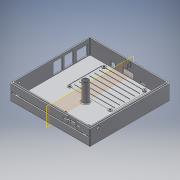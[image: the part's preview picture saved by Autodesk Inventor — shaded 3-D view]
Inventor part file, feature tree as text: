
AUTODESK INVENTOR PART (.ipt)
format: ipt  version: 2018 (Build 220112000, 112)  size: 822,784 bytes
history: native  units: in
note: dims shown in document units (in); Inventor stores cm internally (conversion verified against a paired STEP export)
features: extrude x34, sketch x30, projected_geometry x8, reference x7, fillet x6, plane x6, thread x4, other x3, mirror x1
ambient origin geometry x8: Origin, YZ Plane, XZ Plane, XY Plane, X Axis, Y Axis, Z Axis, Center Point
bodies: Solid1 (feature_tree)
feature tree (99):
  extrude  "Extrusion1"  Depth=4.5in
  extrude  "Extrusion4"  Depth=0.1in
  sketch  "Sketch6"  dims[d12=0.7874in d13=0.0in d17=2.2047in]
  extrude  "Extrusion5"  Depth=2.2047in
  extrude  "Extrusion6"  Depth=0.4035in
  extrude  "Extrusion7"  Depth=0.6299in
  extrude  "Extrusion8"  Depth=0.2589in
  extrude  "Extrusion9"  Depth=0.2589in
  extrude  "Extrusion10"  Depth=0.314in
  extrude  "Extrusion11"  Depth=0.1575in
  extrude  "Extrusion12"  Depth=0.8425in
  thread  "Thread1"  [1 undecoded]
  thread  "Thread2"  [1 undecoded]
  thread  "Thread3"  [1 undecoded]
  thread  "Thread4"  [1 undecoded]
  extrude  "Extrusion13"  Depth=0.689in TaperAngle=0.0deg
  extrude  "Extrusion14"  Depth=0.2953in TaperAngle=0.0deg
  extrude  "Extrusion15"  Depth=0.1378in TaperAngle=0.0deg
  fillet  "Fillet1"  Radius=0.0394in
  extrude  "Extrusion16"  Depth=0.1378in
  extrude  "Extrusion17"  Depth=0.1378in
  fillet  "Fillet3"  Radius=0.1378in
  extrude  "Extrusion18"  Depth=2.2835in
  extrude  "Extrusion19"  Depth=2.2835in
  plane  "Work Plane1"
  extrude  "Extrusion20"  Depth=0.05in
  extrude  "Extrusion21"  Depth=0.05in
  fillet  "Fillet4"  Radius=0.05in
  plane  "Work Plane2"
  extrude  "Extrusion22"  Depth=0.075in TaperAngle=0.0deg
  extrude  "Extrusion23"  Depth=1.0in TaperAngle=0.0deg
  extrude  "Extrusion24"  Depth=1.0in TaperAngle=0.0deg
  extrude  "Extrusion25"  Depth=0.064in
  extrude  "Extrusion26"  Depth=0.05in
  extrude  "Extrusion27"  Depth=0.05in TaperAngle=0.0deg
  extrude  "Extrusion28"  Depth=0.05in TaperAngle=0.0deg
  extrude  "Extrusion29"  Depth=0.05in
  plane  "Work Plane3"
  mirror  "Mirror1"
  sketch  "Sketch27"  dims[d82=0.05in d83=0.0in d84=0.075in]
  plane  "Work Plane4"
  extrude  "Extrusion30"  Depth=0.05in
  extrude  "Extrusion31"  Depth=0.05in TaperAngle=0.0deg
  extrude  "Extrusion32"  Depth=0.05in
  fillet  "Fillet5"  Radius=0.05in
  extrude  "Extrusion33"  Depth=0.05in
  extrude  "Extrusion34"  Depth=0.05in
  sketch  "Sketch32"  dims[d97=0.05in d98=0.05in d99=0.0in]
  plane  "Work Plane5"
  extrude  "Extrusion35"  Depth=0.05in
  fillet  "Fillet6"  [1 undecoded]
  sketch  "Sketch33"  dims[d100=0.175in d101=0.175in d102=0.05in d103=0.0in d104=0.05in d105=0.0875in d106=0.2in d107=90.0deg d108=0.9449in d109=0.0275in d110=0.0275in d111=0.0275in d112=0.9174in d115=0.05in d116=0.0in d117=0.25in d118=0.25in d119=0.05in d120=0.05in d121=0.0in d122=0.05in d123=0.025in d124=0.025in d125=0.025in d126=0.025in d127=0.075in d128=0.3in d129=0.0in d130=0.3in d131=0.0in d132=0.05in d133=0.225in d134=0.1in d135=0.1in d136=0.1in d137=0.025in d138=0.05in d139=0.1in d140=0.1in d141=0.1in d142=0.025in d143=0.05in d144=0.3in d145=0.0in d146=0.05in d147=0.0in d148=0.05in d149=0.0in d150=0.05in d151=0.05in d152=0.05in d153=0.0in d154=0.25in d155=0.25in d156=0.025in d157=0.025in d158=0.25in d159=0.025in d160=0.25in d161=0.025in d162=0.25in d163=0.025in d164=0.25in d165=0.025in d166=0.0125in d167=0.0125in d168=0.05in d169=0.0in d172=0.125in d173=0.125in d174=0.025in d175=0.025in d176=0.0in d177=0.04in d178=0.05in d179=0.0in d180=0.05in d181=0.0in d182=0.0059in d183=0.05in d184=0.01in d185=0.05in d186=0.0in d187=0.01in d188=0.0in d189=0.05in d190=0.0in d191=0.02in d192=0.025in d193=0.025in d194=0.025in d195=0.025in d196=0.025in d197=0.0in d198=0.25in d199=0.25in d200=0.25in d201=0.25in d202=0.25in d203=0.01in d204=0.01in d205=0.01in d206=0.01in d207=0.01in d208=0.0in d209=0.25in d210=0.3in d211=0.025in d212=0.01in d213=0.0in d214=0.05in d215=0.0125in d217=0.0125in d218=0.0125in d219=0.01in d220=0.0in d221=0.05in]
  plane  "Work Plane6"
  extrude  "Extrusion36"  Depth=0.05in
  fillet  "Fillet7"  Radius=0.0275in
  sketch  "Sketch1"  dims[d0=4.5in d1=4.5in]
  sketch  "Sketch4"  dims[d2=0.1in d3=0.0in d11=0.1in]
  projected_geometry  "Projected Loop3"
  sketch  "Sketch7"  dims[d18=3.3465in d21=0.4035in]
  sketch  "Sketch8"  dims[d22=0.7382in d23=0.6299in]
  sketch  "Sketch9"  dims[d24=0.2589in d25=0.2589in]
  projected_geometry  "Projected Loop4"
  projected_geometry  "Projected Loop5"
  projected_geometry  "Projected Loop6"
  sketch  "Sketch10"  dims[d26=0.2589in d27=0.2589in]
  sketch  "Sketch11"  dims[d28=0.314in d29=0.314in]
  sketch  "Sketch12"  dims[d30=0.4173in d31=0.1575in]
  sketch  "Sketch13"  dims[d32=0.1575in d33=0.8425in d34=0.3051in d35=0.3051in d37=0.8465in d38=0.128in]
  sketch  "Sketch14"  dims[d39=0.128in d40=0.689in d41=0.0in]
  sketch  "Sketch15"  dims[d42=0.5906in d43=0.0in d44=0.2953in d45=0.0in]
  sketch  "Sketch16"  dims[d46=0.315in d47=0.0in d48=0.1378in d49=0.0in d50=0.0394in d51=0.0in]
  sketch  "Sketch17"  dims[d52=0.1378in d53=0.1378in]
  sketch  "Sketch18"  dims[d54=0.0925in d56=0.1378in d57=0.1378in]
  projected_geometry  "Projected Loop7"
  sketch  "Sketch19"  dims[d58=0.0925in d59=2.2835in]
  sketch  "Sketch20"  dims[d60=0.0925in d61=2.2835in]
  sketch  "Sketch21"  dims[d62=0.0925in d63=0.05in]
  sketch  "Sketch22"  dims[d64=0.05in d65=0.05in d66=0.05in]
  sketch  "Sketch23"  dims[d67=0.0197in d68=0.0in d69=0.075in d70=0.0in]
  sketch  "Sketch24"  dims[d71=1.0in d72=0.0in d73=1.0in d74=0.0in]
  projected_geometry  "Projected Loop8"
  projected_geometry  "Projected Loop9"
  sketch  "Sketch25"  dims[d75=1.0in d76=0.0in d77=1.0in d78=0.0in]
  reference  "Reference1"
  sketch  "Sketch26"  dims[d79=0.075in d81=0.064in]
  reference  "Reference2"
  reference  "Reference3"
  reference  "Reference4"
  reference  "Reference5"
  sketch  "Sketch28"  dims[d86=0.064in d87=0.05in d88=0.0in]
  projected_geometry  "Projected Loop10"
  sketch  "Sketch29"  dims[d89=0.05in d90=0.05in d91=0.0in]
  sketch  "Sketch30"  dims[d92=0.05in d94=0.45in]
  sketch  "Sketch31"  dims[d95=0.075in d96=0.05in]
  reference  "Reference6"
  reference  "Reference7"
  other  "<userpath>\Documents\Commodore Cube Project\Case\Assembly.iam"
  other  "Assembly.iam"
  other  "Dome:1"
note: 5 required parameter values undecoded (feature->parameter linkage not recoverable at this tier; creation-order binding heuristic only, values carry confidence <= 0.55)
